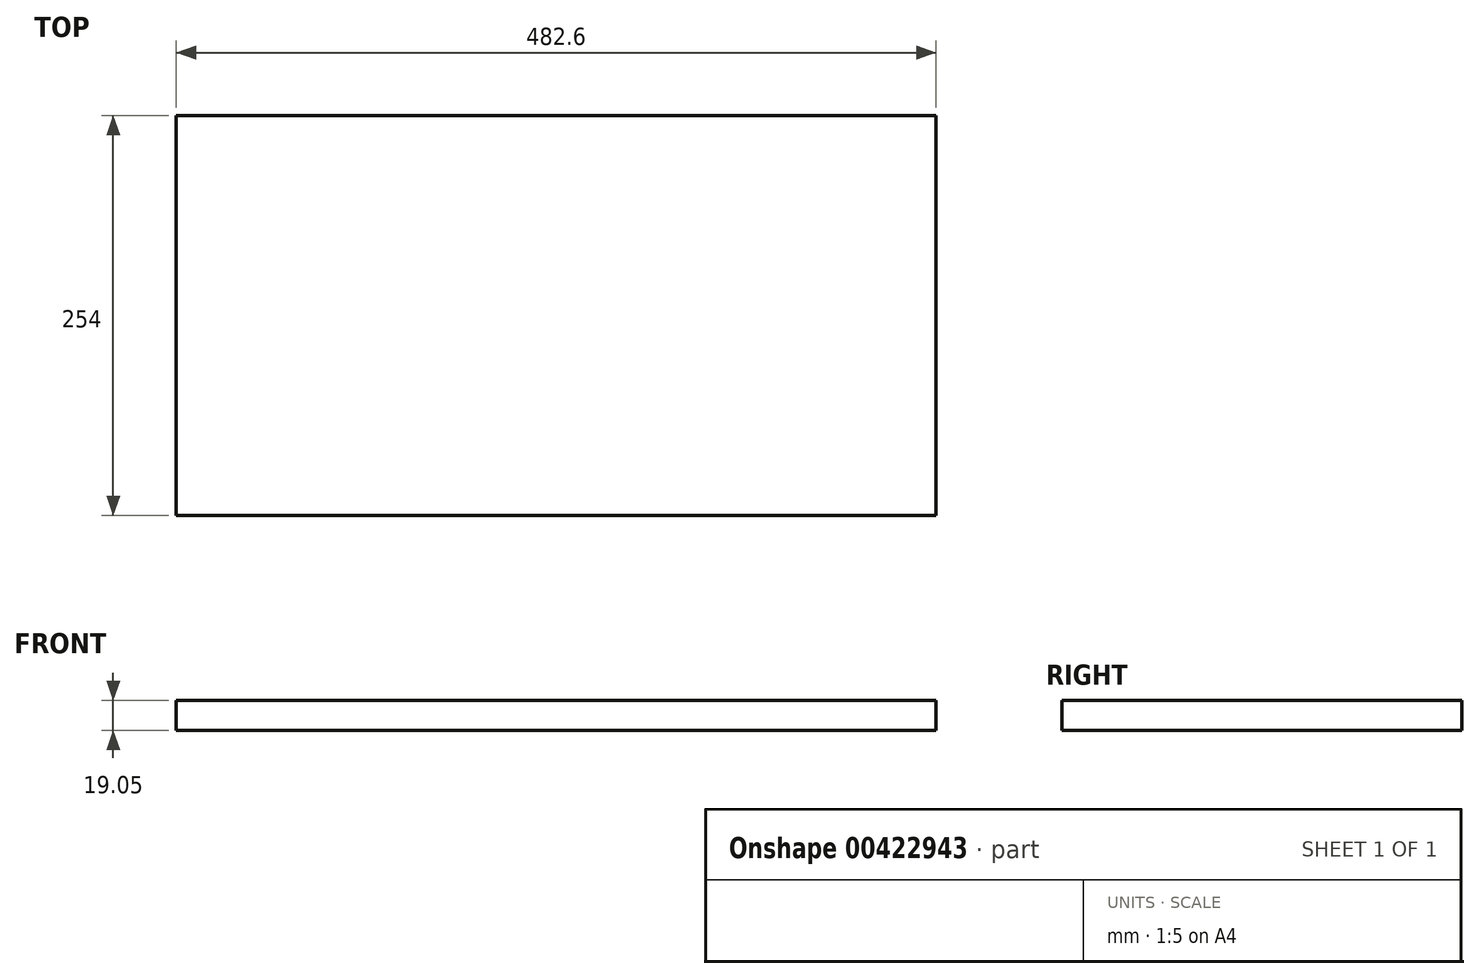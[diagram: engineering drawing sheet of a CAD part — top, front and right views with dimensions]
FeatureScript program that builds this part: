
annotation { "Feature Type Name" : "Feature", "Feature Type Description" : "" }
export const myFeature = defineFeature(function(context is Context, id is Id, definition is map)
    precondition{}
    {
        {
            var Q0;
            Q0=qCreatedBy(makeId("Top.planeOp"),FACE);
            var sketch = newSketch(context, id + "F0", { "sketchPlane" : qUnion([Q0])});
            skLineSegment(sketch, "E0.bottom", {"start": v(241.3, 127) * mm, "end": v(-241.3, 127) * mm});
            skLineSegment(sketch, "E0.top", {"start": v(241.3, -127) * mm, "end": v(-241.3, -127) * mm});
            skLineSegment(sketch, "E0.left", {"start": v(241.3, 127) * mm, "end": v(241.3, -127) * mm});
            skLineSegment(sketch, "E0.right", {"start": v(-241.3, 127) * mm, "end": v(-241.3, -127) * mm});
            skPoint(sketch, "E0.middle", {"position": v(0, 0) * mm});
            skSolve(sketch);
        }
        {
            var Q0;
            Q0 = qSketchRegion(id + "F0", true);
            extrude(context, id + "F1", {"entities" : qUnion([Q0]), "depth" : 19.05 * mm, "offsetDistance" : 25.4 * mm});
        }
    });
